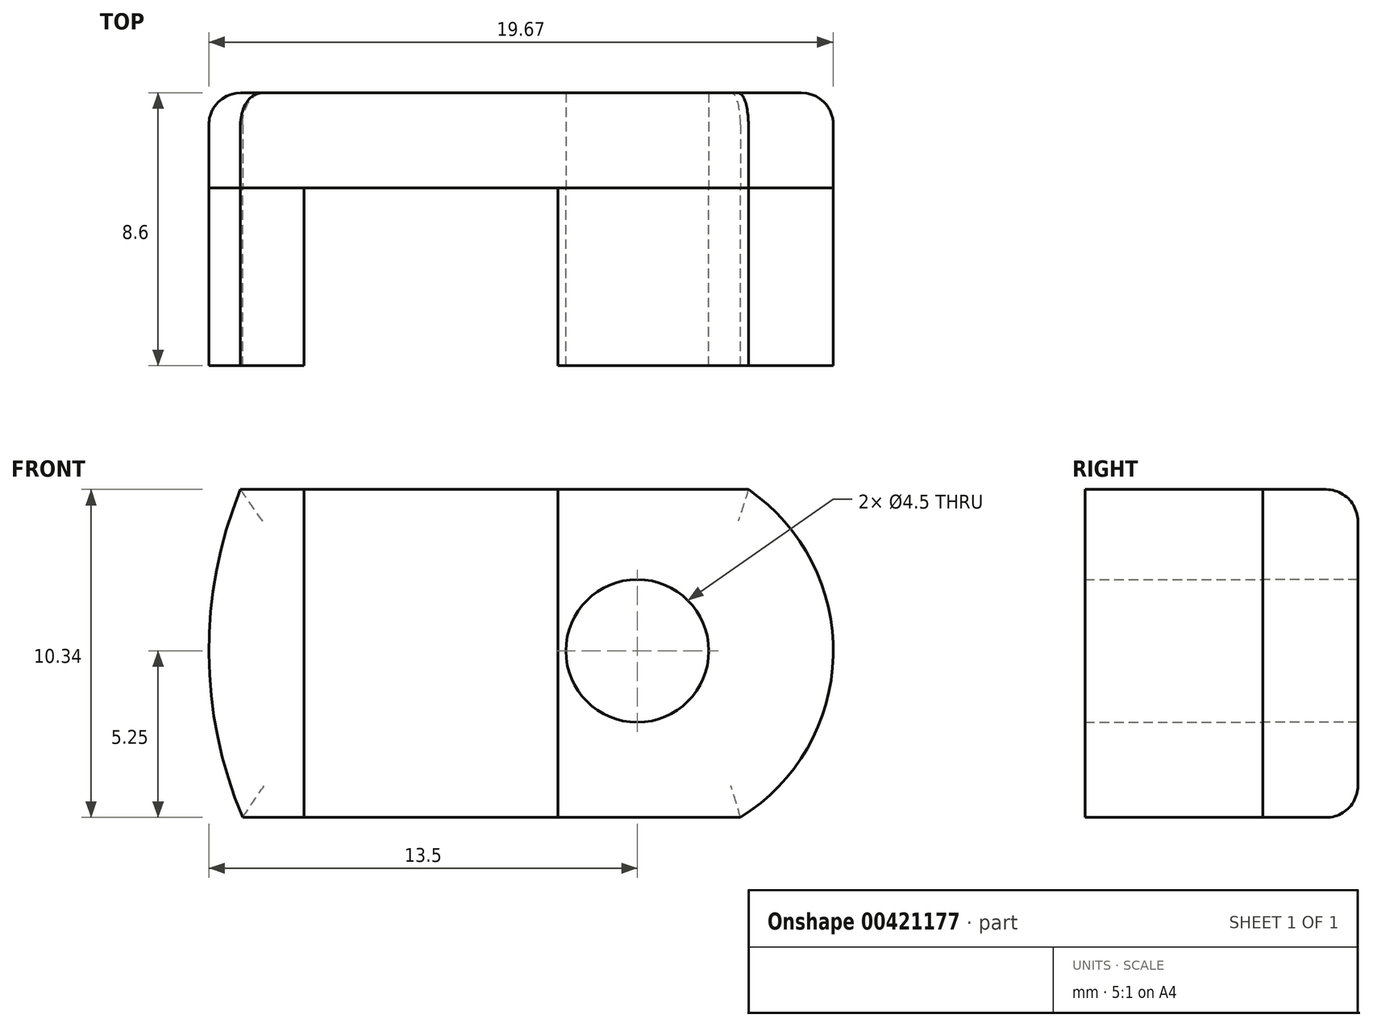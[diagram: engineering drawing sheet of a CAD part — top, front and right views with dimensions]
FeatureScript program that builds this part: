
annotation { "Feature Type Name" : "Feature", "Feature Type Description" : "" }
export const myFeature = defineFeature(function(context is Context, id is Id, definition is map)
    precondition{}
    {
        {
            var Q0;
            Q0=qCreatedBy(makeId("Front.planeOp"),FACE);
            var sketch = newSketch(context, id + "F0", { "sketchPlane" : qUnion([Q0])});
            skCircle(sketch, "E0", {"center": v(0, 0) * mm, "radius": 2.25 * mm});
            skArc(sketch, "E1", {"start": v(-12.5, 5.09) * mm, "mid": v(-13.5, -0.09) * mm, "end": v(-12.44, -5.25) * mm});
            skLineSegment(sketch, "E2", {"start": v(-10.5, 5.09) * mm, "end": v(-10.5, -5.25) * mm});
            skLineSegment(sketch, "E3.0", {"start": v(-2.5, 5.09) * mm, "end": v(-2.5, -5.25) * mm});
            skLineSegment(sketch, "E4", {"start": v(-12.5, 5.09) * mm, "end": v(3.5, 5.09) * mm});
            skLineSegment(sketch, "E5", {"start": v(-12.44, -5.25) * mm, "end": v(3.25, -5.25) * mm});
            skArc(sketch, "E6", {"start": v(3.25, -5.25) * mm, "mid": v(6.17, -0.15) * mm, "end": v(3.5, 5.09) * mm});
            skSolve(sketch);
        }
        {
            var Q0;
            {var subQ0=sQuery(id+"F0.wireOp",EDGE,"E1");Q0=makeQuery(id+"F0.imprint","IMPRINT",FACE,{"disambiguationData":[TD([[makeQuery(id+"F0.imprint","IMPRINT",EDGE,{"derivedFrom":subQ0}),1.0]])]});}
            var Q1;
            Q1=makeQuery(id+"F0.imprint","IMPRINT",FACE,{"disambiguationData":[TD([[makeQuery(id+"F0.imprint","IMPRINT",EDGE,{"derivedFrom":sQuery(id+"F0.wireOp",EDGE,"E0")}),-1.0]])]});
            extrude(context, id + "F1", {"entities" : qUnion([Q0, Q1]), "depth" : 5.6 * mm});
        }
        {
            var Q0;
            {var subQ0=sQuery(id+"F0.wireOp",EDGE,"E1");Q0=makeQuery(id+"F0.imprint","IMPRINT",FACE,{"disambiguationData":[TD([[makeQuery(id+"F0.imprint","IMPRINT",EDGE,{"derivedFrom":subQ0}),1.0]])]});}
            var Q1;
            {var subQ0=sQuery(id+"F0.wireOp",EDGE,"E2");Q1=makeQuery(id+"F0.imprint","IMPRINT",FACE,{"disambiguationData":[TD([[makeQuery(id+"F0.imprint","IMPRINT",EDGE,{"derivedFrom":subQ0}),1.0]])]});}
            var Q2;
            Q2=makeQuery(id+"F0.imprint","IMPRINT",FACE,{"disambiguationData":[TD([[makeQuery(id+"F0.imprint","IMPRINT",EDGE,{"derivedFrom":sQuery(id+"F0.wireOp",EDGE,"E0")}),-1.0]])]});
            extrude(context, id + "F2", {"entities" : qUnion([Q0, Q1, Q2]), "oppositeDirection" : true, "depth" : 3 * mm});
        }
        {
            var Q0;
            Q0=makeQuery(id+"F2.opExtrude","CAP_EDGE",EDGE,{"disambiguationData":[OSD([sQuery(id+"F0.wireOp",EDGE,"E1")])],"isStart":false});
            var Q1;
            Q1=makeQuery(id+"F2.opExtrude","CAP_EDGE",EDGE,{"disambiguationData":[OSD([sQuery(id+"F0.wireOp",EDGE,"E5")])],"isStart":false});
            var Q2;
            Q2=makeQuery(id+"F2.opExtrude","CAP_EDGE",EDGE,{"disambiguationData":[OSD([sQuery(id+"F0.wireOp",EDGE,"E4")])],"isStart":false});
            var Q3;
            Q3=makeQuery(id+"F2.opExtrude","CAP_EDGE",EDGE,{"disambiguationData":[OSD([sQuery(id+"F0.wireOp",EDGE,"E6")])],"isStart":false});
            fillet(context, id + "F3", {"entities" : qUnion([Q0, Q1, Q2, Q3]), "radius" : 1 * mm, "tangentPropagation" : true, "allowEdgeOverflow" : false});
        }
    });
